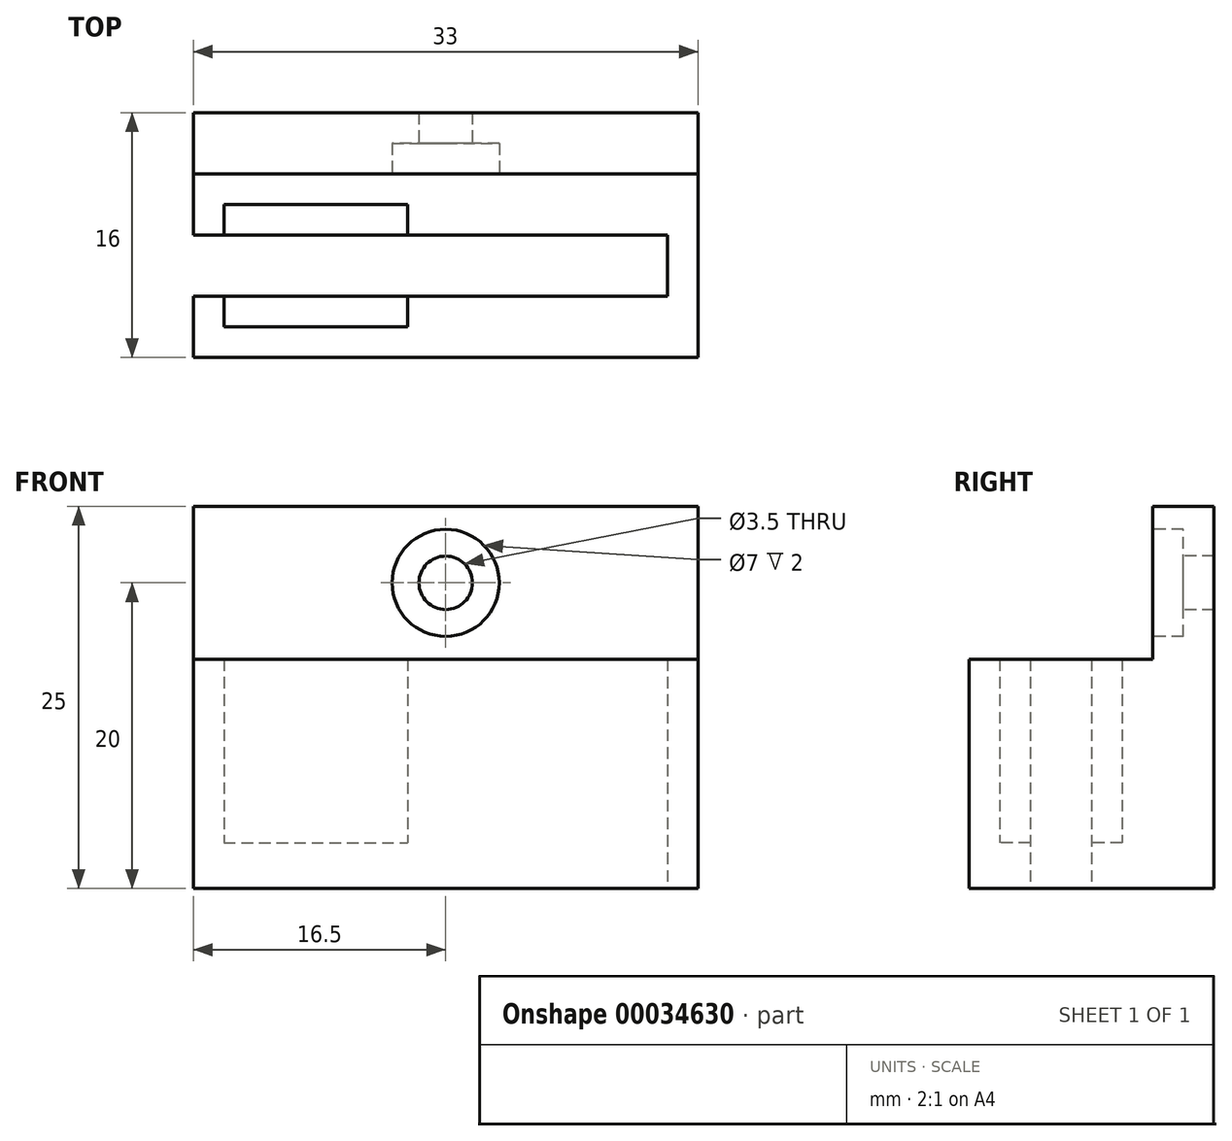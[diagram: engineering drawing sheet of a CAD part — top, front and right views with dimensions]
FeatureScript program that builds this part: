
annotation { "Feature Type Name" : "Feature", "Feature Type Description" : "" }
export const myFeature = defineFeature(function(context is Context, id is Id, definition is map)
    precondition{}
    {
        {
            var Q0;
            Q0=qCreatedBy(makeId("Top.planeOp"),FACE);
            var sketch = newSketch(context, id + "F0", { "sketchPlane" : qUnion([Q0])});
            skLineSegment(sketch, "E0.bottom", {"start": v(0, 0) * mm, "end": v(33, 0) * mm});
            skLineSegment(sketch, "E0.top", {"start": v(0, 12) * mm, "end": v(33, 12) * mm});
            skLineSegment(sketch, "E0.left", {"start": v(0, 0) * mm, "end": v(0, 12) * mm});
            skLineSegment(sketch, "E0.right", {"start": v(33, 0) * mm, "end": v(33, 12) * mm});
            skLineSegment(sketch, "E1.bottom", {"start": v(14, 8) * mm, "end": v(31, 8) * mm});
            skLineSegment(sketch, "E1.top", {"start": v(14, 4) * mm, "end": v(31, 4) * mm});
            skLineSegment(sketch, "E1.left", {"start": v(14, 8) * mm, "end": v(14, 4) * mm});
            skLineSegment(sketch, "E1.right", {"start": v(31, 8) * mm, "end": v(31, 4) * mm});
            skLineSegment(sketch, "E2.bottom", {"start": v(2, 10) * mm, "end": v(14, 10) * mm});
            skLineSegment(sketch, "E2.top", {"start": v(2, 2) * mm, "end": v(14, 2) * mm});
            skLineSegment(sketch, "E2.left", {"start": v(2, 10) * mm, "end": v(2, 2) * mm});
            skLineSegment(sketch, "E2.right", {"start": v(14, 10) * mm, "end": v(14, 2) * mm});
            skLineSegment(sketch, "E3.bottom", {"start": v(0, 8) * mm, "end": v(2, 8) * mm});
            skLineSegment(sketch, "E3.top", {"start": v(0, 4) * mm, "end": v(2, 4) * mm});
            skLineSegment(sketch, "E3.left", {"start": v(0, 8) * mm, "end": v(0, 4) * mm});
            skLineSegment(sketch, "E3.right", {"start": v(2, 8) * mm, "end": v(2, 4) * mm});
            skLineSegment(sketch, "E4.top", {"start": v(0, 16) * mm, "end": v(33, 16) * mm});
            skLineSegment(sketch, "E4.left", {"start": v(0, 12) * mm, "end": v(0, 16) * mm});
            skLineSegment(sketch, "E4.right", {"start": v(33, 12) * mm, "end": v(33, 16) * mm});
            skLineSegment(sketch, "E5", {"start": v(2, 8) * mm, "end": v(14, 8) * mm});
            skLineSegment(sketch, "E6", {"start": v(14, 4) * mm, "end": v(2, 4) * mm});
            skSolve(sketch);
        }
        {
            var Q0;
            Q0=makeQuery(id+"F0.imprint","IMPRINT",FACE,{"disambiguationData":[TD([[makeQuery(id+"F0.imprint","IMPRINT",EDGE,{"derivedFrom":sQuery(id+"F0.wireOp",EDGE,"E0.top")}),1.0]])]});
            extrude(context, id + "F1", {"entities" : qUnion([Q0]), "depth" : 25 * mm});
        }
        {
            var Q0;
            {var subQ2=sQuery(id+"F0.wireOp",EDGE,"E2.bottom");Q0=makeQuery(id+"F0.imprint","IMPRINT",FACE,{"disambiguationData":[TD([[makeQuery(id+"F0.imprint","IMPRINT",EDGE,{"derivedFrom":subQ2}),-1.0]])]});}
            var Q1;
            {var subQ2=sQuery(id+"F0.wireOp",EDGE,"E2.top");Q1=makeQuery(id+"F0.imprint","IMPRINT",FACE,{"disambiguationData":[TD([[makeQuery(id+"F0.imprint","IMPRINT",EDGE,{"derivedFrom":subQ2}),1.0]])]});}
            extrude(context, id + "F2", {"entities" : qUnion([Q0, Q1]), "operationType" : NewBodyOperationType.ADD, "depth" : 3 * mm});
        }
        {
            var Q0;
            {var subQ12=sQuery(id+"F0.wireOp",EDGE,"E0.bottom");Q0=makeQuery(id+"F0.imprint","IMPRINT",FACE,{"disambiguationData":[TD([[makeQuery(id+"F0.imprint","IMPRINT",EDGE,{"derivedFrom":subQ12}),1.0]])]});}
            extrude(context, id + "F3", {"entities" : qUnion([Q0]), "operationType" : NewBodyOperationType.ADD, "depth" : 15 * mm});
        }
        {
            var Q0;
            Q0=makeQuery(id+"F1.opExtrude","SWEPT_FACE",FACE,{"disambiguationData":[OSD([sQuery(id+"F0.wireOp",EDGE,"E0.top")])]});
            var sketch = newSketch(context, id + "F4", { "sketchPlane" : qUnion([Q0])});
            skCircle(sketch, "E7", {"center": v(16.5, 20) * mm, "radius": 3.5 * mm});
            skCircle(sketch, "E8", {"center": v(16.5, 20) * mm, "radius": 1.75 * mm});
            skSolve(sketch);
        }
        {
            var Q0;
            Q0=makeQuery(id+"F4.imprint","IMPRINT",FACE,{"disambiguationData":[TD([[makeQuery(id+"F4.imprint","IMPRINT",EDGE,{"derivedFrom":sQuery(id+"F4.wireOp",EDGE,"E8")}),1.0]])]});
            extrude(context, id + "F5", {"entities" : qUnion([Q0]), "operationType" : NewBodyOperationType.REMOVE, "oppositeDirection" : true, "depth" : 25 * mm});
        }
        {
            var Q0;
            Q0=makeQuery(id+"F4.imprint","IMPRINT",FACE,{"disambiguationData":[TD([[makeQuery(id+"F4.imprint","IMPRINT",EDGE,{"derivedFrom":sQuery(id+"F4.wireOp",EDGE,"E7")}),1.0]])]});
            extrude(context, id + "F6", {"entities" : qUnion([Q0]), "operationType" : NewBodyOperationType.REMOVE, "oppositeDirection" : true, "depth" : 2 * mm});
        }
    });
